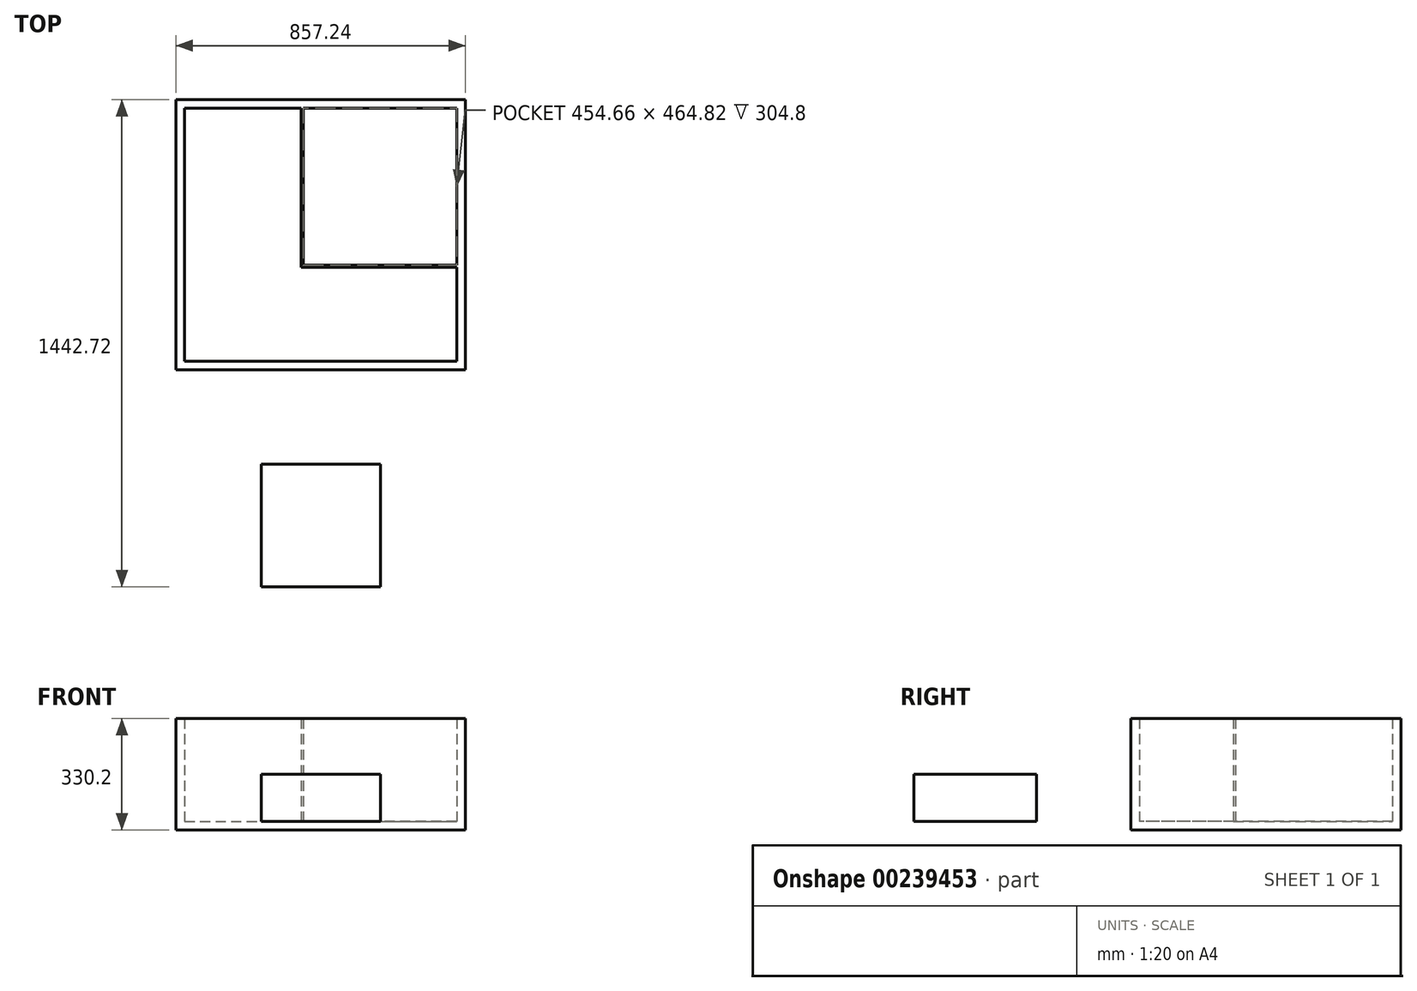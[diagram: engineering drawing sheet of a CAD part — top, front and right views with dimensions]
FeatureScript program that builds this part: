
annotation { "Feature Type Name" : "Feature", "Feature Type Description" : "" }
export const myFeature = defineFeature(function(context is Context, id is Id, definition is map)
    precondition{}
    {
        {
            var Q0;
            Q0=qCreatedBy(makeId("Top.planeOp"),FACE);
            var sketch = newSketch(context, id + "F0", { "sketchPlane" : qUnion([Q0])});
            skLineSegment(sketch, "E0.bottom", {"start": v(-403.23, 749.3) * mm, "end": v(403.23, 749.3) * mm});
            skLineSegment(sketch, "E0.top", {"start": v(-403.23, 0) * mm, "end": v(403.23, 0) * mm});
            skLineSegment(sketch, "E0.left", {"start": v(-403.23, 749.3) * mm, "end": v(-403.23, 0) * mm});
            skLineSegment(sketch, "E0.right", {"start": v(403.23, 749.3) * mm, "end": v(403.22, 0) * mm});
            skLineSegment(sketch, "E1.0", {"start": v(428.63, 774.7) * mm, "end": v(428.63, -25.4) * mm});
            skLineSegment(sketch, "E1.1", {"start": v(-428.63, 774.7) * mm, "end": v(428.63, 774.7) * mm});
            skLineSegment(sketch, "E1.2", {"start": v(-428.63, 774.7) * mm, "end": v(-428.63, -25.4) * mm});
            skLineSegment(sketch, "E1.3", {"start": v(-428.63, -25.4) * mm, "end": v(428.63, -25.4) * mm});
            skSolve(sketch);
        }
        {
            var Q0;
            Q0=makeQuery(id+"F0.imprint","IMPRINT",FACE,{"disambiguationData":[TD([[makeQuery(id+"F0.imprint","IMPRINT",EDGE,{"derivedFrom":sQuery(id+"F0.wireOp",EDGE,"E0.bottom")}),1.0]])]});
            extrude(context, id + "F1", {"entities" : qUnion([Q0]), "depth" : 304.8 * mm});
        }
        {
            var Q0;
            Q0=makeQuery(id+"F0.imprint","IMPRINT",FACE,{"disambiguationData":[TD([[makeQuery(id+"F0.imprint","IMPRINT",EDGE,{"derivedFrom":sQuery(id+"F0.wireOp",EDGE,"E0.bottom")}),-1.0]])]});
            var Q1;
            Q1=makeQuery(id+"F0.imprint","IMPRINT",FACE,{"disambiguationData":[TD([[makeQuery(id+"F0.imprint","IMPRINT",EDGE,{"derivedFrom":sQuery(id+"F0.wireOp",EDGE,"E0.bottom")}),1.0]])]});
            extrude(context, id + "F2", {"entities" : qUnion([Q0, Q1]), "operationType" : NewBodyOperationType.ADD, "oppositeDirection" : true, "depth" : 25.4 * mm});
        }
        {
            var Q0;
            Q0=qCreatedBy(makeId("Top.planeOp"),FACE);
            var sketch = newSketch(context, id + "F3", { "sketchPlane" : qUnion([Q0])});
            skLineSegment(sketch, "E2.bottom", {"start": v(176.53, -668.02) * mm, "end": v(-176.53, -668.02) * mm});
            skLineSegment(sketch, "E2.top", {"start": v(176.53, -304.8) * mm, "end": v(-176.53, -304.8) * mm});
            skLineSegment(sketch, "E2.left", {"start": v(176.53, -668.02) * mm, "end": v(176.53, -304.8) * mm});
            skLineSegment(sketch, "E2.right", {"start": v(-176.53, -668.02) * mm, "end": v(-176.53, -304.8) * mm});
            skLineSegment(sketch, "E3", {"start": v(0, 0) * mm, "end": v(0, -304.8) * mm, "construction": true});
            skSolve(sketch);
        }
        {
            var Q0;
            Q0 = qSketchRegion(id + "F3", true);
            extrude(context, id + "F4", {"entities" : qUnion([Q0]), "depth" : 139.7 * mm});
        }
        {
            var Q0;
            Q0=makeQuery(id+"F0.imprint","IMPRINT",FACE,{"disambiguationData":[TD([[makeQuery(id+"F0.imprint","IMPRINT",EDGE,{"derivedFrom":sQuery(id+"F0.wireOp",EDGE,"E0.bottom")}),-1.0]])]});
            var sketch = newSketch(context, id + "F5", { "sketchPlane" : qUnion([Q0])});
            skLineSegment(sketch, "E4.bottom", {"start": v(403.23, 278.13) * mm, "end": v(-57.79, 278.13) * mm});
            skLineSegment(sketch, "E4.top", {"start": v(403.23, 284.48) * mm, "end": v(-51.44, 284.48) * mm});
            skLineSegment(sketch, "E4.left", {"start": v(403.23, 278.13) * mm, "end": v(403.23, 284.48) * mm});
            skLineSegment(sketch, "E4.right", {"start": v(-57.79, 278.13) * mm, "end": v(-57.79, 284.48) * mm});
            skLineSegment(sketch, "E5.bottom", {"start": v(-57.79, 278.13) * mm, "end": v(-51.44, 278.13) * mm});
            skLineSegment(sketch, "E5.top", {"start": v(-57.79, 749.3) * mm, "end": v(-51.44, 749.3) * mm});
            skLineSegment(sketch, "E5.left", {"start": v(-57.79, 278.13) * mm, "end": v(-57.79, 749.3) * mm});
            skLineSegment(sketch, "E5.right", {"start": v(-51.44, 284.48) * mm, "end": v(-51.44, 749.3) * mm});
            skSolve(sketch);
        }
        {
            var Q0;
            Q0 = qSketchRegion(id + "F5", true);
            var Q1;
            Q1=makeQuery(id+"F1.opExtrude","CAP_FACE",FACE,{"disambiguationData":[OSD([sQuery(id+"F0.wireOp",EDGE,"E0.bottom"),sQuery(id+"F0.wireOp",EDGE,"E0.top"),sQuery(id+"F0.wireOp",EDGE,"E0.left"),sQuery(id+"F0.wireOp",EDGE,"E0.right"),sQuery(id+"F0.wireOp",EDGE,"E1.0"),sQuery(id+"F0.wireOp",EDGE,"E1.1"),sQuery(id+"F0.wireOp",EDGE,"E1.2"),sQuery(id+"F0.wireOp",EDGE,"E1.3")])],"isStart":false});
            extrude(context, id + "F6", {"entities" : qUnion([Q0]), "operationType" : NewBodyOperationType.ADD, "endBound" : BoundingType.UP_TO_SURFACE, "endBoundEntityFace" : qUnion([Q1]), "depth" : 25.4 * mm});
        }
    });
